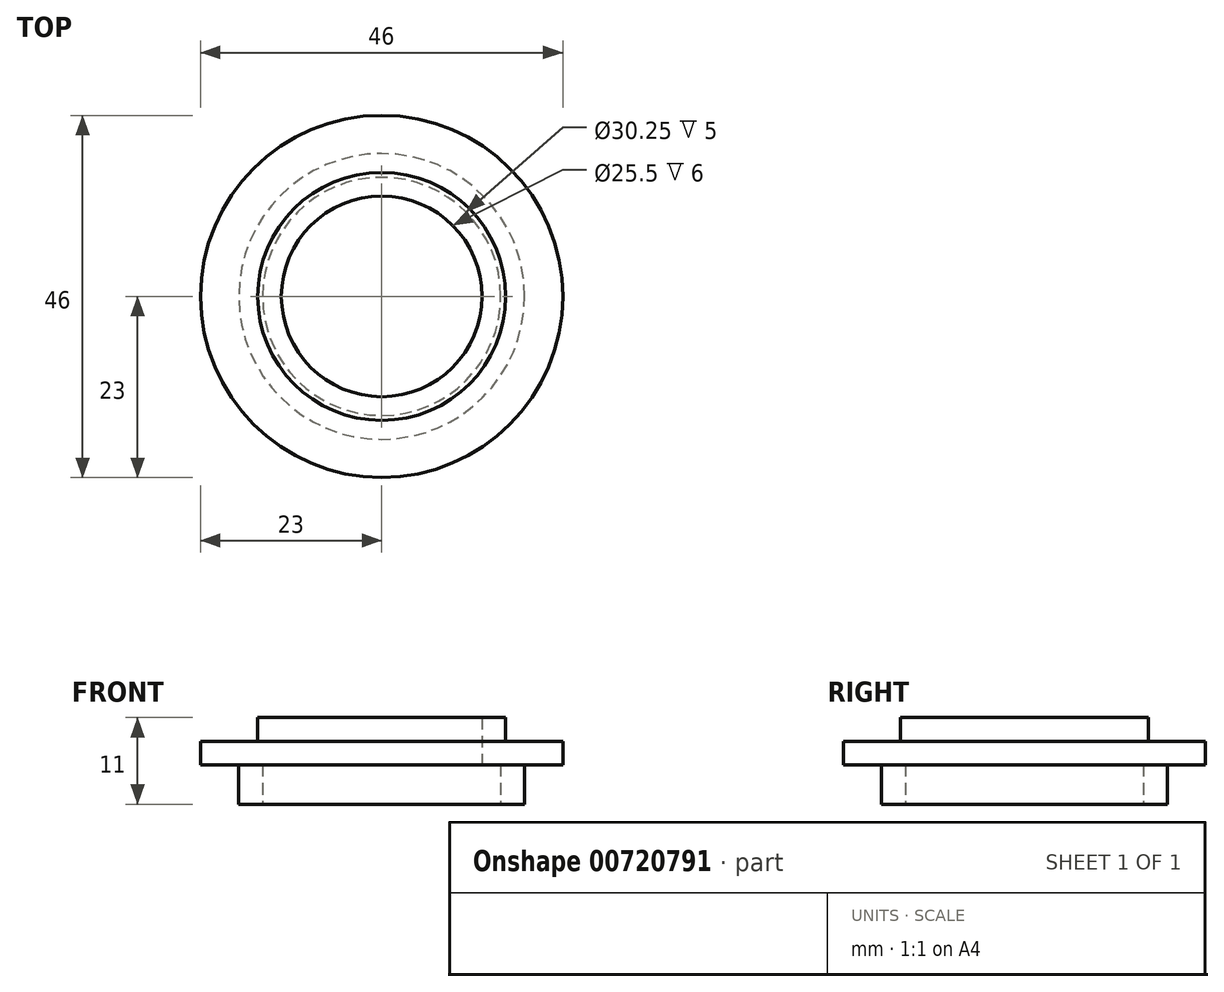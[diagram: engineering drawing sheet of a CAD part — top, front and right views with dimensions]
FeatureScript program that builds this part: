
annotation { "Feature Type Name" : "Feature", "Feature Type Description" : "" }
export const myFeature = defineFeature(function(context is Context, id is Id, definition is map)
    precondition{}
    {
        {
            var Q0;
            Q0=qCreatedBy(makeId("Top.planeOp"),FACE);
            var sketch = newSketch(context, id + "F0", { "sketchPlane" : qUnion([Q0])});
            skCircle(sketch, "E0", {"center": v(0, 0) * mm, "radius": 15.12 * mm});
            skCircle(sketch, "E1", {"center": v(0, 0) * mm, "radius": 18.15 * mm});
            skSolve(sketch);
        }
        {
            var Q0;
            Q0=makeQuery(id+"F0.imprint","IMPRINT",FACE,{"disambiguationData":[TD([[makeQuery(id+"F0.imprint","IMPRINT",EDGE,{"derivedFrom":sQuery(id+"F0.wireOp",EDGE,"E0")}),-1.0]])]});
            extrude(context, id + "F1", {"entities" : qUnion([Q0]), "depth" : 5 * mm, "offsetDistance" : 25 * mm});
        }
        {
            var Q0;
            Q0=makeQuery(id+"F1.opExtrude","CAP_FACE",FACE,{"disambiguationData":[OSD([sQuery(id+"F0.wireOp",EDGE,"E0"),sQuery(id+"F0.wireOp",EDGE,"E1")])],"isStart":false});
            var sketch = newSketch(context, id + "F2", { "sketchPlane" : qUnion([Q0])});
            skCircle(sketch, "E2", {"center": v(0, 0) * mm, "radius": 23 * mm});
            skCircle(sketch, "E3", {"center": v(0, 0) * mm, "radius": 12.75 * mm});
            skSolve(sketch);
        }
        {
            var Q0;
            Q0=makeQuery(id+"F2.imprint","IMPRINT",FACE,{"disambiguationData":[TD([[makeQuery(id+"F2.imprint","IMPRINT",EDGE,{"derivedFrom":sQuery(id+"F2.wireOp",EDGE,"E2")}),1.0]])]});
            var Q1;
            Q1=makeQuery(id+"F2.imprint","IMPRINT",FACE,{"disambiguationData":[TD([[makeQuery(id+"F2.imprint","IMPRINT",EDGE,{"derivedFrom":sQuery(id+"F2.wireOp",EDGE,"E3")}),-1.0]])]});
            var Q2;
            Q2=makeQuery(id+"F2.imprint","IMPRINT",FACE,{"disambiguationData":[TD([[makeQuery(id+"F2.imprint","IMPRINT",EDGE,{"derivedFrom":makeQuery(id+"F1.opExtrude","CAP_EDGE",EDGE,{"disambiguationData":[OSD([sQuery(id+"F0.wireOp",EDGE,"E0")])],"isStart":false})}),-1.0]])]});
            extrude(context, id + "F3", {"entities" : qUnion([Q0, Q1, Q2]), "operationType" : NewBodyOperationType.ADD, "depth" : 3 * mm, "offsetDistance" : 25 * mm});
        }
        {
            var Q0;
            Q0=makeQuery(id+"F3.opExtrude","CAP_FACE",FACE,{"disambiguationData":[OSD([sQuery(id+"F2.wireOp",EDGE,"E2"),sQuery(id+"F2.wireOp",EDGE,"E3")])],"isStart":false});
            var sketch = newSketch(context, id + "F4", { "sketchPlane" : qUnion([Q0])});
            skCircle(sketch, "E4", {"center": v(0, 0) * mm, "radius": 15.75 * mm});
            skSolve(sketch);
        }
        {
            var Q0;
            Q0=makeQuery(id+"F4.imprint","IMPRINT",FACE,{"disambiguationData":[TD([[makeQuery(id+"F4.imprint","IMPRINT",EDGE,{"derivedFrom":sQuery(id+"F4.wireOp",EDGE,"E4")}),1.0]])]});
            extrude(context, id + "F5", {"entities" : qUnion([Q0]), "operationType" : NewBodyOperationType.ADD, "depth" : 3 * mm, "offsetDistance" : 25 * mm});
        }
    });
